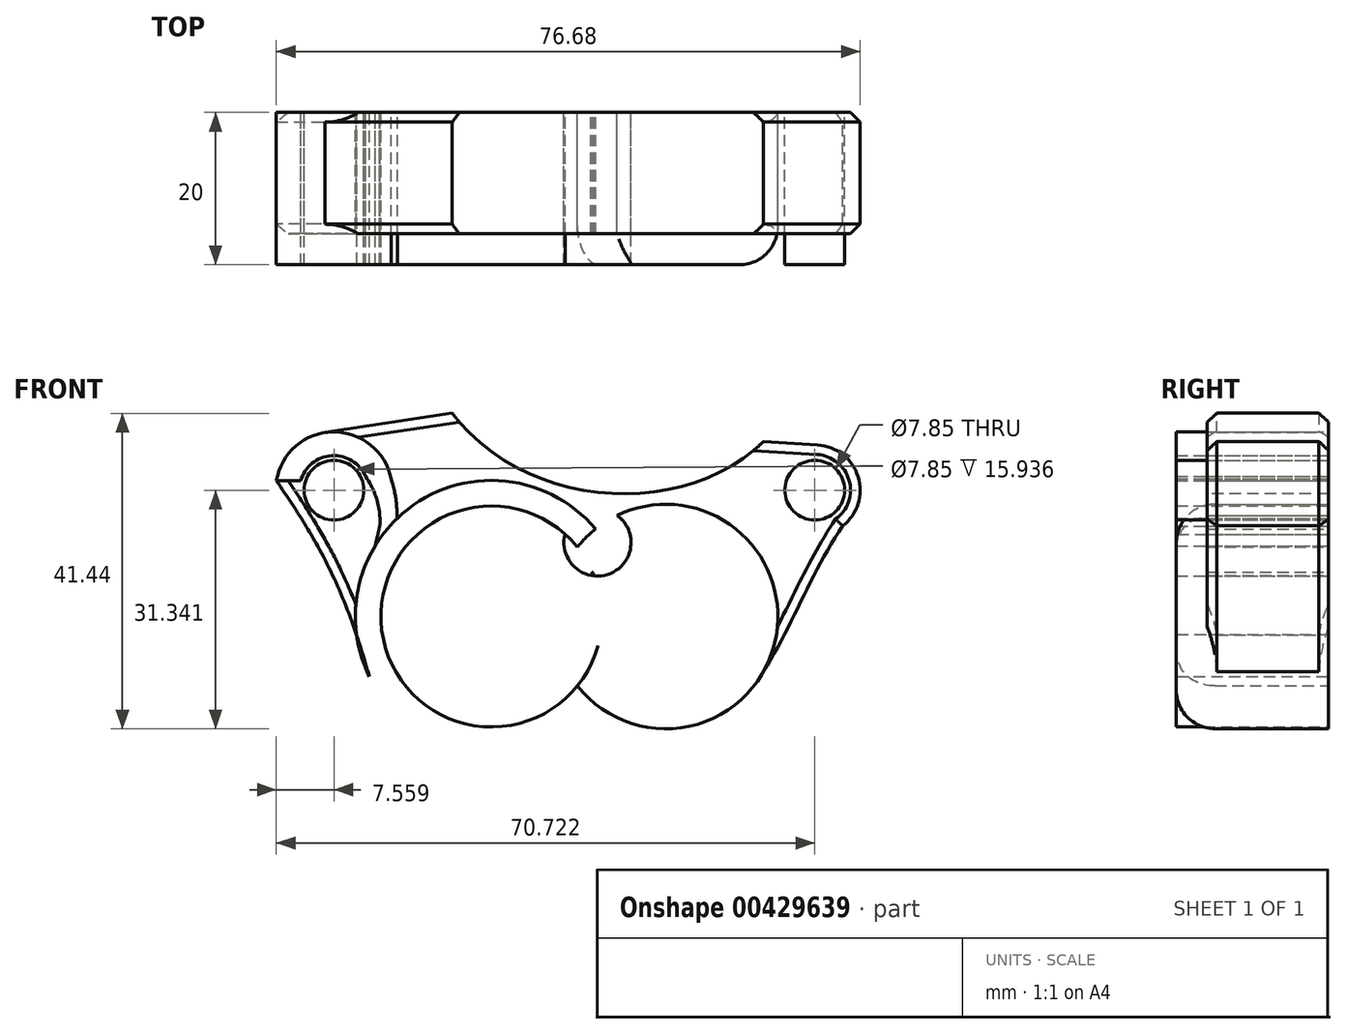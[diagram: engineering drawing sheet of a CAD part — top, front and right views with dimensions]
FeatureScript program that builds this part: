
annotation { "Feature Type Name" : "Feature", "Feature Type Description" : "" }
export const myFeature = defineFeature(function(context is Context, id is Id, definition is map)
    precondition{}
    {
        {
            var Q0;
            Q0=qCreatedBy(makeId("Front.planeOp"),FACE);
            var sketch = newSketch(context, id + "F0", { "sketchPlane" : qUnion([Q0])});
            skCircle(sketch, "E0", {"center": v(0, 0) * mm, "radius": 4.4 * mm});
            skCircle(sketch, "E1", {"center": v(8.96, -9.72) * mm, "radius": 11.24 * mm});
            skCircle(sketch, "E2", {"center": v(8.96, -9.72) * mm, "radius": 14.74 * mm});
            skCircle(sketch, "E3", {"center": v(-13.93, -9.72) * mm, "radius": 14.51 * mm});
            skCircle(sketch, "E4", {"center": v(-34.62, 6.88) * mm, "radius": 4.54 * mm});
            skCircle(sketch, "E5", {"center": v(-13.93, -9.72) * mm, "radius": 17.87 * mm});
            skCircle(sketch, "E6", {"center": v(28.54, 6.88) * mm, "radius": 5.96 * mm});
            skCircle(sketch, "E7", {"center": v(-34.62, 6.88) * mm, "radius": 7.66 * mm});
            skFitSpline(sketch, "E8", {"points": [v(32.22, 2.19) * mm, v(20.82, -18.47) * mm], "startDerivative": vector(-13.14, -19.41) * mm, "endDerivative": vector(-13.14, -19.41) * mm});
            skLineSegment(sketch, "E9", {"start": v(-35.77, 14.45) * mm, "end": v(-19.07, 16.98) * mm});
            skLineSegment(sketch, "E10", {"start": v(28.92, 12.83) * mm, "end": v(21.8, 13.28) * mm});
            skFitSpline(sketch, "E11", {"points": [v(-19.07, 16.98) * mm, v(21.8, 13.28) * mm], "startDerivative": vector(29.5, -38.9) * mm, "endDerivative": vector(30.6, 30.08) * mm});
            skCircle(sketch, "E12", {"center": v(28.54, 6.88) * mm, "radius": 4.54 * mm});
            skFitSpline(sketch, "E13", {"points": [v(-42.18, 8.1) * mm, v(-29.98, -17.6) * mm], "startDerivative": vector(16.86, -24.32) * mm, "endDerivative": vector(9.4, -33.85) * mm});
            skCircle(sketch, "E14", {"center": v(-34.62, 6.88) * mm, "radius": 3.93 * mm});
            skCircle(sketch, "E15", {"center": v(28.54, 6.88) * mm, "radius": 3.93 * mm});
            skFitSpline(sketch, "E16", {"points": [v(-28.6, 2.14) * mm, v(-29.2, -0.43) * mm], "startDerivative": vector(-0.59, -2.58) * mm, "endDerivative": vector(-0.59, -2.58) * mm});
            skFitSpline(sketch, "E17", {"points": [v(-28.6, 2.14) * mm, v(-30.45, 8.67) * mm], "startDerivative": vector(0.5, 6) * mm, "endDerivative": vector(-4.48, 6.46) * mm});
            skFitSpline(sketch, "E18", {"points": [v(-26.3, 3.2) * mm, v(-27.1, 8.35) * mm], "startDerivative": vector(-0.29, 6.73) * mm, "endDerivative": vector(-2.12, 7.31) * mm});
            skLineSegment(sketch, "E19", {"start": v(-39, 8.1) * mm, "end": v(-42.18, 8.1) * mm});
            skSolve(sketch);
        }
        {
            var Q0;
            {var subQ0=sQuery(id+"F0.wireOp",EDGE,"E8");var subQ1=sQuery(id+"F0.wireOp",EDGE,"E2");var subQ2=makeQuery(id+"F0.imprint","INTERSECT",VERTEX,{"disambiguationData":[OD(0.0)],"derivedFrom":[subQ1,subQ0]});Q0=makeQuery(id+"F0.imprint","IMPRINT",FACE,{"disambiguationData":[TD([[makeQuery(id+"F0.imprint","IMPRINT",EDGE,{"disambiguationData":[TD([[subQ2,-1.0]])],"derivedFrom":subQ1}),1.0]])]});}
            var Q1;
            {var subQ0=sQuery(id+"F0.wireOp",EDGE,"E13");var subQ1=sQuery(id+"F0.wireOp",EDGE,"E5");var subQ2=makeQuery(id+"F0.imprint","INTERSECT",VERTEX,{"disambiguationData":[OD(0.0)],"derivedFrom":[subQ1,subQ0]});Q1=makeQuery(id+"F0.imprint","IMPRINT",FACE,{"disambiguationData":[TD([[makeQuery(id+"F0.imprint","IMPRINT",EDGE,{"disambiguationData":[TD([[subQ2,1.0]])],"derivedFrom":subQ1}),1.0]])]});}
            var Q2;
            {var subQ0=sQuery(id+"F0.wireOp",EDGE,"E3");var subQ1=sQuery(id+"F0.wireOp",EDGE,"E1");var subQ2=makeQuery(id+"F0.imprint","INTERSECT",VERTEX,{"disambiguationData":[OD(1.0)],"derivedFrom":[subQ1,subQ0]});Q2=makeQuery(id+"F0.imprint","IMPRINT",FACE,{"disambiguationData":[TD([[makeQuery(id+"F0.imprint","IMPRINT",EDGE,{"disambiguationData":[TD([[subQ2,-1.0]])],"derivedFrom":subQ1}),-1.0]])]});}
            var Q3;
            {var subQ1=sQuery(id+"F0.wireOp",EDGE,"E5");var subQ3=sQuery(id+"F0.wireOp",EDGE,"E0");var subQ4=makeQuery(id+"F0.imprint","INTERSECT",VERTEX,{"disambiguationData":[OD(0.0)],"derivedFrom":[subQ3,subQ1]});Q3=makeQuery(id+"F0.imprint","IMPRINT",FACE,{"disambiguationData":[TD([[makeQuery(id+"F0.imprint","IMPRINT",EDGE,{"disambiguationData":[TD([[subQ4,-1.0]])],"derivedFrom":subQ3}),-1.0]])]});}
            var Q4;
            {var subQ0=sQuery(id+"F0.wireOp",EDGE,"E2");var subQ5=sQuery(id+"F0.wireOp",EDGE,"E0");var subQ12=makeQuery(id+"F0.imprint","INTERSECT",VERTEX,{"disambiguationData":[OD(0.0)],"derivedFrom":[subQ5,subQ0]});Q4=makeQuery(id+"F0.imprint","IMPRINT",FACE,{"disambiguationData":[TD([[makeQuery(id+"F0.imprint","IMPRINT",EDGE,{"disambiguationData":[TD([[subQ12,1.0]])],"derivedFrom":subQ5}),-1.0]])]});}
            var Q5;
            {var subQ0=sQuery(id+"F0.wireOp",EDGE,"ca57e5a5-9555-4379-9683-af36b6f8ddd0");Q5=makeQuery(id+"F0.imprint","IMPRINT",FACE,{"disambiguationData":[TD([[makeQuery(id+"F0.imprint","IMPRINT",EDGE,{"derivedFrom":subQ0}),-1.0]])]});}
            var Q6;
            {var subQ0=sQuery(id+"F0.wireOp",EDGE,"E3");var subQ1=sQuery(id+"F0.wireOp",EDGE,"E0");var subQ2=makeQuery(id+"F0.imprint","INTERSECT",VERTEX,{"disambiguationData":[OD(0.0)],"derivedFrom":[subQ1,subQ0]});Q6=makeQuery(id+"F0.imprint","IMPRINT",FACE,{"disambiguationData":[TD([[makeQuery(id+"F0.imprint","IMPRINT",EDGE,{"disambiguationData":[TD([[subQ2,-1.0]])],"derivedFrom":subQ1}),-1.0]])]});}
            var Q7;
            {var subQ0=sQuery(id+"F0.wireOp",EDGE,"E2");var subQ1=sQuery(id+"F0.wireOp",EDGE,"E0");var subQ2=makeQuery(id+"F0.imprint","INTERSECT",VERTEX,{"disambiguationData":[OD(1.0)],"derivedFrom":[subQ1,subQ0]});Q7=makeQuery(id+"F0.imprint","IMPRINT",FACE,{"disambiguationData":[TD([[makeQuery(id+"F0.imprint","IMPRINT",EDGE,{"disambiguationData":[TD([[subQ2,-1.0]])],"derivedFrom":subQ1}),-1.0]])]});}
            var Q8;
            {var subQ0=sQuery(id+"F0.wireOp",EDGE,"E1");var subQ1=sQuery(id+"F0.wireOp",EDGE,"E0");var subQ2=makeQuery(id+"F0.imprint","INTERSECT",VERTEX,{"disambiguationData":[OD(1.0)],"derivedFrom":[subQ1,subQ0]});Q8=makeQuery(id+"F0.imprint","IMPRINT",FACE,{"disambiguationData":[TD([[makeQuery(id+"F0.imprint","IMPRINT",EDGE,{"disambiguationData":[TD([[subQ2,-1.0]])],"derivedFrom":subQ1}),-1.0]])]});}
            var Q9;
            {var subQ0=sQuery(id+"F0.wireOp",EDGE,"E3");var subQ1=sQuery(id+"F0.wireOp",EDGE,"E0");var subQ2=makeQuery(id+"F0.imprint","INTERSECT",VERTEX,{"disambiguationData":[OD(1.0)],"derivedFrom":[subQ1,subQ0]});Q9=makeQuery(id+"F0.imprint","IMPRINT",FACE,{"disambiguationData":[TD([[makeQuery(id+"F0.imprint","IMPRINT",EDGE,{"disambiguationData":[TD([[subQ2,-1.0]])],"derivedFrom":subQ1}),-1.0]])]});}
            var Q10;
            {var subQ0=sQuery(id+"F0.wireOp",EDGE,"E1");var subQ1=sQuery(id+"F0.wireOp",EDGE,"E0");var subQ2=makeQuery(id+"F0.imprint","INTERSECT",VERTEX,{"disambiguationData":[OD(0.0)],"derivedFrom":[subQ1,subQ0]});Q10=makeQuery(id+"F0.imprint","IMPRINT",FACE,{"disambiguationData":[TD([[makeQuery(id+"F0.imprint","IMPRINT",EDGE,{"disambiguationData":[TD([[subQ2,1.0]])],"derivedFrom":subQ1}),-1.0]])]});}
            var Q11;
            {var subQ0=sQuery(id+"F0.wireOp",EDGE,"E16");Q11=makeQuery(id+"F0.imprint","IMPRINT",FACE,{"disambiguationData":[TD([[makeQuery(id+"F0.imprint","IMPRINT",EDGE,{"derivedFrom":subQ0}),1.0]])]});}
            var Q12;
            {var subQ3=sQuery(id+"F0.wireOp",EDGE,"E17");Q12=makeQuery(id+"F0.imprint","IMPRINT",FACE,{"disambiguationData":[TD([[makeQuery(id+"F0.imprint","IMPRINT",EDGE,{"derivedFrom":subQ3}),-1.0]])]});}
            var Q13;
            Q13=makeQuery(id+"F0.imprint","IMPRINT",FACE,{"disambiguationData":[TD([[makeQuery(id+"F0.imprint","IMPRINT",EDGE,{"derivedFrom":sQuery(id+"F0.wireOp",EDGE,"E14")}),1.0]])]});
            var Q14;
            Q14=makeQuery(id+"F0.imprint","IMPRINT",FACE,{"disambiguationData":[TD([[makeQuery(id+"F0.imprint","IMPRINT",EDGE,{"derivedFrom":sQuery(id+"F0.wireOp",EDGE,"E15")}),1.0]])]});
            extrude(context, id + "F1", {"entities" : qUnion([Q0, Q1, Q2, Q3, Q4, Q5, Q6, Q7, Q8, Q9, Q10, Q11, Q12, Q13, Q14]), "depth" : 20 * mm});
        }
        {
            var Q0;
            {var subQ11=sQuery(id+"F0.wireOp",EDGE,"E9");Q0=makeQuery(id+"F0.imprint","IMPRINT",FACE,{"disambiguationData":[TD([[makeQuery(id+"F0.imprint","IMPRINT",EDGE,{"derivedFrom":subQ11}),-1.0]])]});}
            var Q1;
            Q1=makeQuery(id+"F0.imprint","IMPRINT",FACE,{"disambiguationData":[TD([[makeQuery(id+"F0.imprint","IMPRINT",EDGE,{"derivedFrom":sQuery(id+"F0.wireOp",EDGE,"E14")}),-1.0]])]});
            var Q2;
            {var subQ4=sQuery(id+"F0.wireOp",EDGE,"E17");Q2=makeQuery(id+"F0.imprint","IMPRINT",FACE,{"disambiguationData":[TD([[makeQuery(id+"F0.imprint","IMPRINT",EDGE,{"derivedFrom":subQ4}),1.0]])]});}
            var Q3;
            {var subQ0=sQuery(id+"F0.wireOp",EDGE,"E16");Q3=makeQuery(id+"F0.imprint","IMPRINT",FACE,{"disambiguationData":[TD([[makeQuery(id+"F0.imprint","IMPRINT",EDGE,{"derivedFrom":subQ0}),-1.0]])]});}
            var Q4;
            {var subQ0=sQuery(id+"F0.wireOp",EDGE,"E5");var subQ1=sQuery(id+"F0.wireOp",EDGE,"E1");var subQ2=makeQuery(id+"F0.imprint","INTERSECT",VERTEX,{"disambiguationData":[OD(0.0)],"derivedFrom":[subQ1,subQ0]});Q4=makeQuery(id+"F0.imprint","IMPRINT",FACE,{"disambiguationData":[TD([[makeQuery(id+"F0.imprint","IMPRINT",EDGE,{"disambiguationData":[TD([[subQ2,-1.0]])],"derivedFrom":subQ1}),-1.0]])]});}
            var Q5;
            {var subQ0=sQuery(id+"F0.wireOp",EDGE,"E2");var subQ1=sQuery(id+"F0.wireOp",EDGE,"E0");var subQ2=makeQuery(id+"F0.imprint","INTERSECT",VERTEX,{"disambiguationData":[OD(1.0)],"derivedFrom":[subQ1,subQ0]});Q5=makeQuery(id+"F0.imprint","IMPRINT",FACE,{"disambiguationData":[TD([[makeQuery(id+"F0.imprint","IMPRINT",EDGE,{"disambiguationData":[TD([[subQ2,-1.0]])],"derivedFrom":subQ1}),1.0]])]});}
            var Q6;
            {var subQ0=sQuery(id+"F0.wireOp",EDGE,"E3");var subQ1=sQuery(id+"F0.wireOp",EDGE,"E0");var subQ2=makeQuery(id+"F0.imprint","INTERSECT",VERTEX,{"disambiguationData":[OD(0.0)],"derivedFrom":[subQ1,subQ0]});Q6=makeQuery(id+"F0.imprint","IMPRINT",FACE,{"disambiguationData":[TD([[makeQuery(id+"F0.imprint","IMPRINT",EDGE,{"disambiguationData":[TD([[subQ2,-1.0]])],"derivedFrom":subQ1}),1.0]])]});}
            var Q7;
            {var subQ0=sQuery(id+"F0.wireOp",EDGE,"E5");var subQ1=sQuery(id+"F0.wireOp",EDGE,"E0");var subQ2=makeQuery(id+"F0.imprint","INTERSECT",VERTEX,{"disambiguationData":[OD(0.0)],"derivedFrom":[subQ1,subQ0]});Q7=makeQuery(id+"F0.imprint","IMPRINT",FACE,{"disambiguationData":[TD([[makeQuery(id+"F0.imprint","IMPRINT",EDGE,{"disambiguationData":[TD([[subQ2,-1.0]])],"derivedFrom":subQ1}),1.0]])]});}
            var Q8;
            {var subQ0=sQuery(id+"F0.wireOp",EDGE,"E2");var subQ1=sQuery(id+"F0.wireOp",EDGE,"E0");var subQ2=makeQuery(id+"F0.imprint","INTERSECT",VERTEX,{"disambiguationData":[OD(0.0)],"derivedFrom":[subQ1,subQ0]});Q8=makeQuery(id+"F0.imprint","IMPRINT",FACE,{"disambiguationData":[TD([[makeQuery(id+"F0.imprint","IMPRINT",EDGE,{"disambiguationData":[TD([[subQ2,-1.0]])],"derivedFrom":subQ1}),1.0]])]});}
            var Q9;
            {var subQ0=sQuery(id+"F0.wireOp",EDGE,"E2");var subQ1=sQuery(id+"F0.wireOp",EDGE,"E0");var subQ2=makeQuery(id+"F0.imprint","INTERSECT",VERTEX,{"disambiguationData":[OD(0.0)],"derivedFrom":[subQ1,subQ0]});Q9=makeQuery(id+"F0.imprint","IMPRINT",FACE,{"disambiguationData":[TD([[makeQuery(id+"F0.imprint","IMPRINT",EDGE,{"disambiguationData":[TD([[subQ2,1.0]])],"derivedFrom":subQ1}),1.0]])]});}
            var Q10;
            {var subQ0=sQuery(id+"F0.wireOp",EDGE,"E3");var subQ1=sQuery(id+"F0.wireOp",EDGE,"E0");var subQ2=makeQuery(id+"F0.imprint","INTERSECT",VERTEX,{"disambiguationData":[OD(1.0)],"derivedFrom":[subQ1,subQ0]});Q10=makeQuery(id+"F0.imprint","IMPRINT",FACE,{"disambiguationData":[TD([[makeQuery(id+"F0.imprint","IMPRINT",EDGE,{"disambiguationData":[TD([[subQ2,-1.0]])],"derivedFrom":subQ1}),1.0]])]});}
            var Q11;
            {var subQ0=sQuery(id+"F0.wireOp",EDGE,"E1");var subQ1=sQuery(id+"F0.wireOp",EDGE,"E0");var subQ2=makeQuery(id+"F0.imprint","INTERSECT",VERTEX,{"disambiguationData":[OD(0.0)],"derivedFrom":[subQ1,subQ0]});Q11=makeQuery(id+"F0.imprint","IMPRINT",FACE,{"disambiguationData":[TD([[makeQuery(id+"F0.imprint","IMPRINT",EDGE,{"disambiguationData":[TD([[subQ2,1.0]])],"derivedFrom":subQ1}),1.0]])]});}
            var Q12;
            Q12=makeQuery(id+"F0.imprint","IMPRINT",FACE,{"disambiguationData":[TD([[makeQuery(id+"F0.imprint","IMPRINT",EDGE,{"derivedFrom":sQuery(id+"F0.wireOp",EDGE,"E12")}),-1.0]])]});
            var Q13;
            Q13=makeQuery(id+"F0.imprint","IMPRINT",FACE,{"disambiguationData":[TD([[makeQuery(id+"F0.imprint","IMPRINT",EDGE,{"derivedFrom":sQuery(id+"F0.wireOp",EDGE,"E12")}),1.0]])]});
            extrude(context, id + "F2", {"entities" : qUnion([Q0, Q1, Q2, Q3, Q4, Q5, Q6, Q7, Q8, Q9, Q10, Q11, Q12, Q13]), "depth" : 15.94 * mm});
        }
        {
            var Q0;
            {var subQ0=sQuery(id+"F0.wireOp",EDGE,"LTu0nikh-84gW-nAeV-L56u-Fk67s8YSFbhU");var subQ1=sQuery(id+"F0.wireOp",EDGE,"E2");Q0=makeQuery(id+"F63nfAjoKkGU20C_5.boolean.opBoolean","SPLIT",EDGE,{"disambiguationData":[TD([makeQuery(id+"F63nfAjoKkGU20C_5.opExtrude","SWEPT_FACE",FACE,{"disambiguationData":[OSD([subQ0])]})])],"derivedFrom":makeQuery(id+"F1.opExtrude","CAP_EDGE",EDGE,{"disambiguationData":[OSD([subQ1])],"isStart":false})});}
            var Q1;
            {var subQ1=sQuery(id+"F0.wireOp",EDGE,"E2");var subQ3=sQuery(id+"F0.wireOp",EDGE,"E0");Q1=makeQuery(id+"F63nfAjoKkGU20C_5.boolean.opBoolean","SPLIT",EDGE,{"disambiguationData":[TD([makeQuery(id+"F1.opExtrude","SWEPT_FACE",FACE,{"disambiguationData":[OSD([subQ3])]})])],"derivedFrom":makeQuery(id+"F1.opExtrude","CAP_EDGE",EDGE,{"disambiguationData":[OSD([subQ1])],"isStart":false})});}
            var Q2;
            {var subQ0=sQuery(id+"F0.wireOp",EDGE,"E5");Q2=makeQuery(id+"F1.opExtrude","CAP_EDGE",EDGE,{"disambiguationData":[OSD([subQ0]),TDD([makeQuery(id+"F0.imprint","IMPRINT",EDGE,{"disambiguationData":[TD([[makeQuery(id+"F0.imprint","INTERSECT",VERTEX,{"derivedFrom":[subQ0,sQuery(id+"F0.wireOp",EDGE,"E18")]}),1.0]])],"derivedFrom":subQ0})])],"isStart":false});}
            var Q3;
            Q3=makeQuery(id+"F63nfAjoKkGU20C_5.opExtrude","CAP_EDGE",EDGE,{"disambiguationData":[OSD([sQuery(id+"F0.wireOp",EDGE,"LTu0nikh-84gW-nAeV-L56u-Fk67s8YSFbhU")])],"isStart":false});
            fillet(context, id + "F3", {"entities" : qUnion([Q0, Q1, Q2, Q3]), "radius" : 5.08 * mm, "tangentPropagation" : true, "allowEdgeOverflow" : false});
        }
        {
            var Q0;
            Q0=makeQuery(id+"F2.opExtrude","CAP_EDGE",EDGE,{"disambiguationData":[OSD([sQuery(id+"F0.wireOp",EDGE,"E13")])],"isStart":false});
            var Q1;
            Q1=makeQuery(id+"F2.opExtrude","CAP_EDGE",EDGE,{"disambiguationData":[OSD([sQuery(id+"F0.wireOp",EDGE,"E8")])],"isStart":false});
            var Q2;
            Q2=makeQuery(id+"F2.opExtrude","CAP_EDGE",EDGE,{"disambiguationData":[OSD([sQuery(id+"F0.wireOp",EDGE,"E9")])],"isStart":false});
            var Q3;
            Q3=makeQuery(id+"F2.opExtrude","CAP_EDGE",EDGE,{"disambiguationData":[OSD([sQuery(id+"F0.wireOp",EDGE,"E9")])],"isStart":true});
            var Q4;
            Q4=makeQuery(id+"F2.opExtrude","CAP_EDGE",EDGE,{"disambiguationData":[OSD([sQuery(id+"F0.wireOp",EDGE,"E13")])],"isStart":true});
            var Q5;
            Q5=makeQuery(id+"F2.opExtrude","CAP_EDGE",EDGE,{"disambiguationData":[OSD([sQuery(id+"F0.wireOp",EDGE,"E10")])],"isStart":true});
            var Q6;
            Q6=makeQuery(id+"F2.opExtrude","CAP_EDGE",EDGE,{"disambiguationData":[OSD([sQuery(id+"F0.wireOp",EDGE,"E10")])],"isStart":false});
            var Q7;
            Q7=makeQuery(id+"F2.opExtrude","CAP_EDGE",EDGE,{"disambiguationData":[OSD([sQuery(id+"F0.wireOp",EDGE,"E8")])],"isStart":true});
            chamfer(context, id + "F4", {"entities" : qUnion([Q0, Q1, Q2, Q3, Q4, Q5, Q6, Q7]), "width" : 1.27 * mm, "tangentPropagation" : true});
        }
    });
